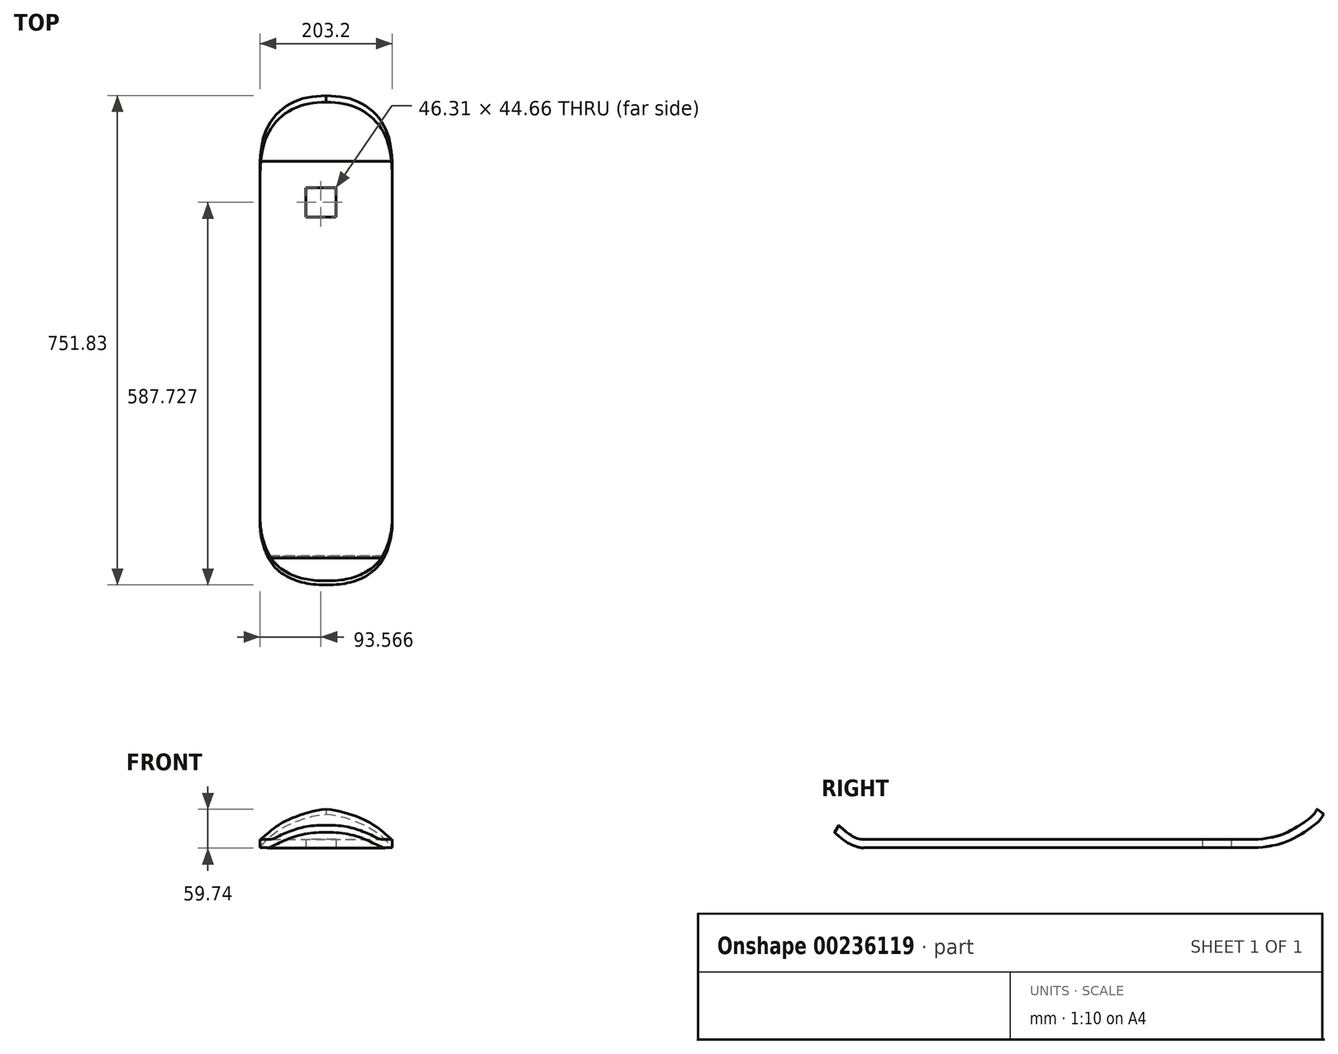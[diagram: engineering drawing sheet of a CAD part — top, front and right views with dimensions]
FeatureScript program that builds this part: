
annotation { "Feature Type Name" : "Feature", "Feature Type Description" : "" }
export const myFeature = defineFeature(function(context is Context, id is Id, definition is map)
    precondition{}
    {
        {
            var Q0;
            Q0=qCreatedBy(makeId("Top.planeOp"),FACE);
            var sketch = newSketch(context, id + "F0", { "sketchPlane" : qUnion([Q0])});
            skLineSegment(sketch, "E0.bottom", {"start": v(-101.6, 304.8) * mm, "end": v(101.6, 304.8) * mm});
            skLineSegment(sketch, "E0.top", {"start": v(-101.6, -304.8) * mm, "end": v(101.6, -304.8) * mm});
            skLineSegment(sketch, "E0.left", {"start": v(-101.6, 304.8) * mm, "end": v(-101.6, -304.8) * mm});
            skLineSegment(sketch, "E0.right", {"start": v(101.6, 304.8) * mm, "end": v(101.6, -304.8) * mm});
            skPoint(sketch, "E0.middle", {"position": v(0, 0) * mm});
            skLineSegment(sketch, "E1.bottom", {"start": v(15.12, 219.15) * mm, "end": v(-31.19, 219.15) * mm});
            skLineSegment(sketch, "E1.top", {"start": v(15.12, 263.8) * mm, "end": v(-31.19, 263.8) * mm});
            skLineSegment(sketch, "E1.left", {"start": v(15.12, 219.15) * mm, "end": v(15.12, 263.8) * mm});
            skLineSegment(sketch, "E1.right", {"start": v(-31.19, 219.15) * mm, "end": v(-31.19, 263.8) * mm});
            skPoint(sketch, "E1.middle", {"position": v(-8.03, 241.48) * mm});
            skSolve(sketch);
        }
        {
            var Q0;
            Q0=makeQuery(id+"F0.imprint","IMPRINT",FACE,{"disambiguationData":[TD([[makeQuery(id+"F0.imprint","IMPRINT",EDGE,{"derivedFrom":sQuery(id+"F0.wireOp",EDGE,"E0.bottom")}),-1.0]])]});
            extrude(context, id + "F1", {"entities" : qUnion([Q0]), "endBound" : BoundingType.SYMMETRIC, "depth" : 12.7 * mm});
        }
        {
            var Q0;
            Q0=qCreatedBy(makeId("Right.planeOp"),FACE);
            var sketch = newSketch(context, id + "F2", { "sketchPlane" : qUnion([Q0])});
            skFitSpline(sketch, "E2", {"points": [v(304.82, 0) * mm, v(339, 6.52) * mm, v(364.5, 18.37) * mm, v(392.94, 38.52) * mm, v(400.64, 49.2) * mm], "startDerivative": vector(127.15, 18.32) * mm, "endDerivative": vector(32.1, 57.84) * mm});
            skFitSpline(sketch, "E3", {"points": [v(-302.08, 0) * mm, v(-311.8, 2.36) * mm, v(-321.84, 6.93) * mm, v(-333.73, 15.44) * mm, v(-342.8, 23.3) * mm], "startDerivative": vector(-42.72, 8.79) * mm, "endDerivative": vector(-34.24, 30.72) * mm});
            skSolve(sketch);
        }
        {
            var Q0;
            Q0=makeQuery(id+"F1.opExtrude","SWEPT_FACE",FACE,{"disambiguationData":[OSD([sQuery(id+"F0.wireOp",EDGE,"E0.bottom")])]});
            var Q1;
            Q1=sQuery(id+"F2.wireOp",EDGE,"E2");
            sweep(context, id + "F3", {"operationType" : NewBodyOperationType.ADD, "profiles" : qUnion([Q0]), "path" : qUnion([Q1])});
        }
        {
            var Q0;
            Q0=makeQuery(id+"F1.opExtrude","SWEPT_FACE",FACE,{"disambiguationData":[OSD([sQuery(id+"F0.wireOp",EDGE,"E0.top")])]});
            var Q1;
            Q1=sQuery(id+"F2.wireOp",EDGE,"E3");
            sweep(context, id + "F4", {"operationType" : NewBodyOperationType.ADD, "profiles" : qUnion([Q0]), "path" : qUnion([Q1])});
        }
        {
            var Q0;
            Q0=makeQuery(id+"F4.opSweep","CAP_EDGE",EDGE,{"disambiguationData":[OSD([sQuery(id+"F0.wireOp",EDGE,"E0.top"),sQuery(id+"F0.wireOp",EDGE,"E0.right"),sQuery(id+"F2.wireOp",VERTEX,"E3.end")])],"isStart":false});
            var Q1;
            Q1=makeQuery(id+"F4.opSweep","CAP_EDGE",EDGE,{"disambiguationData":[OSD([sQuery(id+"F0.wireOp",EDGE,"E0.top"),sQuery(id+"F0.wireOp",EDGE,"E0.left"),sQuery(id+"F2.wireOp",VERTEX,"E3.end")])],"isStart":false});
            fillet(context, id + "F5", {"entities" : qUnion([Q0, Q1]), "radius" : 95.05 * mm, "tangentPropagation" : true, "allowEdgeOverflow" : false});
        }
        {
            var Q0;
            Q0=makeQuery(id+"F3.opSweep","CAP_EDGE",EDGE,{"disambiguationData":[OSD([sQuery(id+"F0.wireOp",EDGE,"E0.bottom"),sQuery(id+"F0.wireOp",EDGE,"E0.left"),sQuery(id+"F2.wireOp",VERTEX,"E2.end")])],"isStart":false});
            var Q1;
            Q1=makeQuery(id+"F3.opSweep","CAP_EDGE",EDGE,{"disambiguationData":[OSD([sQuery(id+"F0.wireOp",EDGE,"E0.bottom"),sQuery(id+"F0.wireOp",EDGE,"E0.right"),sQuery(id+"F2.wireOp",VERTEX,"E2.end")])],"isStart":false});
            fillet(context, id + "F6", {"entities" : qUnion([Q0, Q1]), "radius" : 108.54 * mm, "tangentPropagation" : true, "allowEdgeOverflow" : false});
        }
    });
